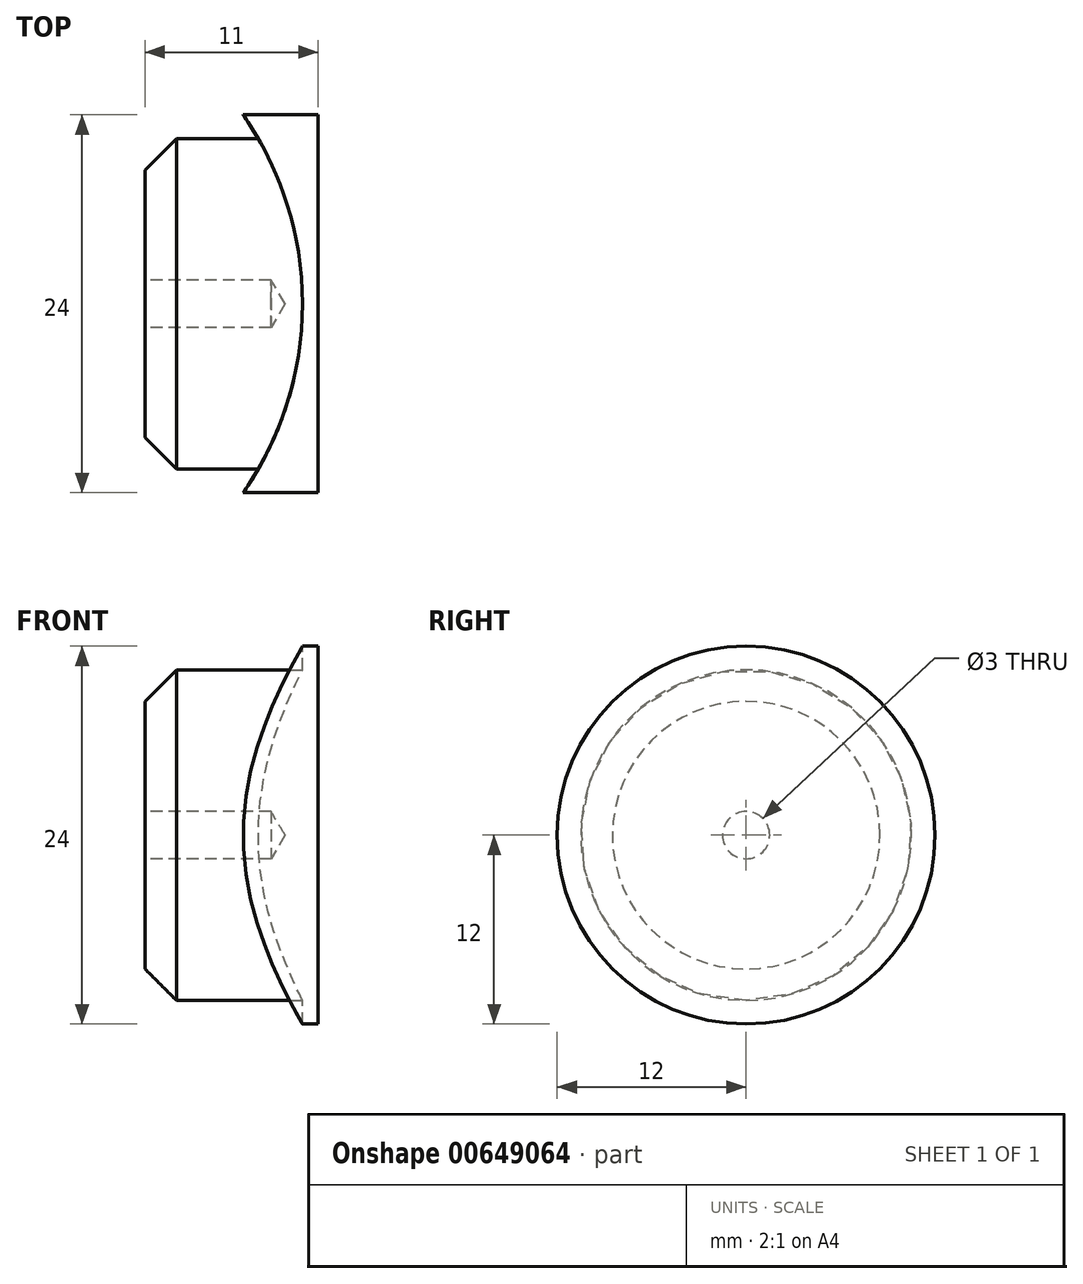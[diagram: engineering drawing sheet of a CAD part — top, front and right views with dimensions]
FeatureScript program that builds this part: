
annotation { "Feature Type Name" : "Feature", "Feature Type Description" : "" }
export const myFeature = defineFeature(function(context is Context, id is Id, definition is map)
    precondition{}
    {
        {
            var Q0;
            Q0=qCreatedBy(makeId("Right.planeOp"),FACE);
            var sketch = newSketch(context, id + "F0", { "sketchPlane" : qUnion([Q0])});
            skCircle(sketch, "E0", {"center": v(0, 0) * mm, "radius": 12 * mm});
            skSolve(sketch);
        }
        {
            var Q0;
            Q0=makeQuery(id+"F0.imprint","IMPRINT",FACE,{"disambiguationData":[TD([[makeQuery(id+"F0.imprint","IMPRINT",EDGE,{"derivedFrom":sQuery(id+"F0.wireOp",EDGE,"E0")}),1.0]])]});
            extrude(context, id + "F1", {"entities" : qUnion([Q0]), "depth" : 5 * mm, "offsetDistance" : 25 * mm});
        }
        {
            var Q0;
            Q0=qCreatedBy(makeId("Top.planeOp"),FACE);
            var sketch = newSketch(context, id + "F2", { "sketchPlane" : qUnion([Q0])});
            skCircle(sketch, "E1", {"center": v(-17, 0) * mm, "radius": 21 * mm});
            skSolve(sketch);
        }
        {
            var Q0;
            Q0=makeQuery(id+"F2.imprint","IMPRINT",FACE,{"disambiguationData":[TD([[makeQuery(id+"F2.imprint","IMPRINT",EDGE,{"derivedFrom":sQuery(id+"F2.wireOp",EDGE,"E1")}),1.0]])]});
            extrude(context, id + "F3", {"entities" : qUnion([Q0]), "operationType" : NewBodyOperationType.REMOVE, "endBound" : BoundingType.THROUGH_ALL, "oppositeDirection" : true, "depth" : 25 * mm, "offsetDistance" : 25 * mm, "hasSecondDirection" : true, "secondDirectionBound" : SecondDirectionBoundingType.THROUGH_ALL, "secondDirectionOppositeDirection" : false, "secondDirectionDepth" : 25 * mm});
        }
        {
            var Q0;
            Q0=qCreatedBy(makeId("Right.planeOp"),FACE);
            var sketch = newSketch(context, id + "F4", { "sketchPlane" : qUnion([Q0])});
            skCircle(sketch, "E2", {"center": v(0, 0) * mm, "radius": 10.5 * mm});
            skSolve(sketch);
        }
        {
            var Q0;
            Q0=qSketchRegion(id+"F4",true);
            extrude(context, id + "F5", {"entities" : qUnion([Q0]), "operationType" : NewBodyOperationType.ADD, "oppositeDirection" : true, "depth" : 6 * mm, "offsetDistance" : 25 * mm, "hasSecondDirection" : true, "secondDirectionBound" : SecondDirectionBoundingType.UP_TO_NEXT, "secondDirectionOppositeDirection" : false, "secondDirectionDepth" : 25 * mm});
        }
        {
            var Q0;
            Q0=makeQuery(id+"F5.opExtrude","CAP_EDGE",EDGE,{"disambiguationData":[OSD([sQuery(id+"F4.wireOp",EDGE,"E2")])],"isStart":false});
            chamfer(context, id + "F6", {"entities" : qUnion([Q0]), "width" : 2 * mm, "tangentPropagation" : true});
        }
        {
            var Q0;
            Q0=makeQuery(id+"F5.opExtrude","CAP_FACE",FACE,{"disambiguationData":[OSD([sQuery(id+"F4.wireOp",EDGE,"E2")])],"isStart":false});
            var sketch = newSketch(context, id + "F7", { "sketchPlane" : qUnion([Q0])});
            skPoint(sketch, "E3", {"position": v(0, 0) * mm});
            skSolve(sketch);
        }
        {
            var Q0;
            Q0=sQuery(id+"F7.wireOp",VERTEX,"E3");
            var Q1;
            Q1=makeQuery(id+"F1.opExtrude","SWEPT_BODY",BODY,{"disambiguationData":[OSD([sQuery(id+"F0.wireOp",EDGE,"E0")])]});
            hole(context, id + "F8", {"style" : HoleStyle.SIMPLE, "endStyle" : HoleEndStyle.BLIND, "holeDiameter" : 3 * mm, "majorDiameter" : 5 * mm, "holeDepth" : 8 * mm, "isTappedThrough" : true, "tappedDepth" : 12 * mm, "tapClearance" : 3, "locations" : qUnion([Q0]), "scope" : qUnion([Q1])});
        }
    });
